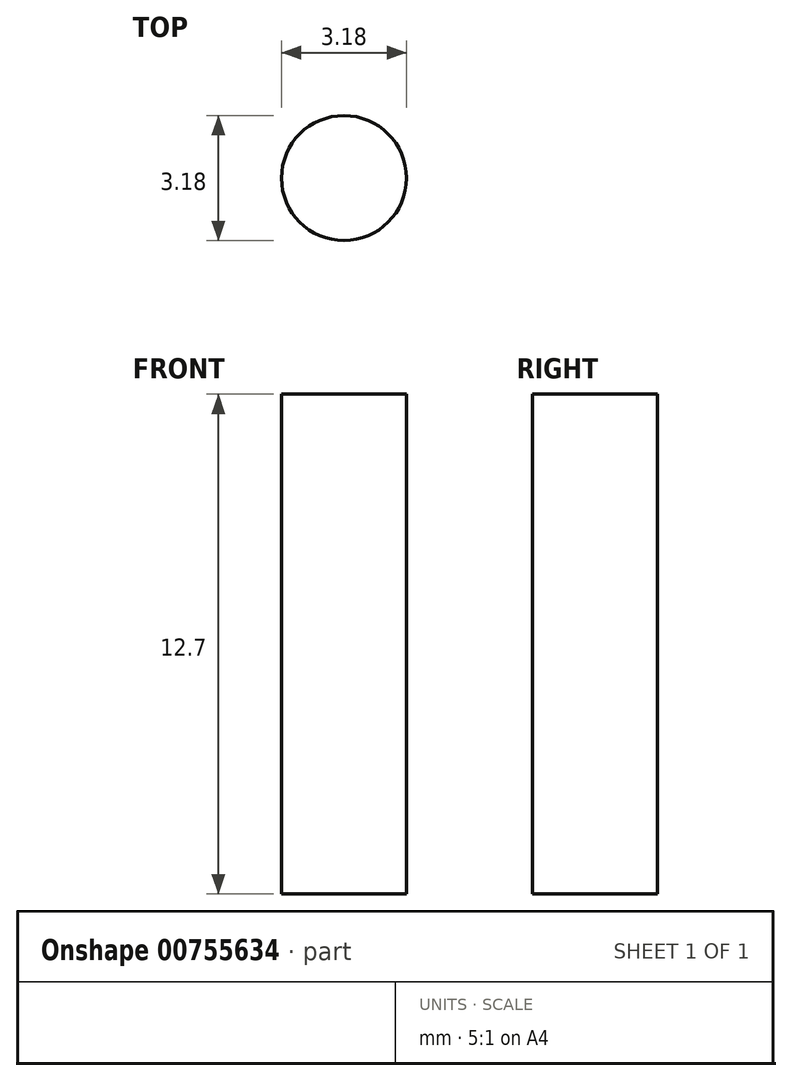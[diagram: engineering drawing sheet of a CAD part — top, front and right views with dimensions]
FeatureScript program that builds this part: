
annotation { "Feature Type Name" : "Feature", "Feature Type Description" : "" }
export const myFeature = defineFeature(function(context is Context, id is Id, definition is map)
    precondition{}
    {
        {
            var Q0;
            Q0=qCreatedBy(makeId("Top.planeOp"),FACE);
            var sketch = newSketch(context, id + "F0", { "sketchPlane" : qUnion([Q0])});
            skCircle(sketch, "E0", {"center": v(-9.14, 0) * mm, "radius": 1.59 * mm});
            skSolve(sketch);
        }
        {
            var Q0;
            Q0=qSketchRegion(id+"F0",true);
            extrude(context, id + "F1", {"entities" : qUnion([Q0]), "depth" : 12.7 * mm, "offsetDistance" : 25.4 * mm});
        }
    });
